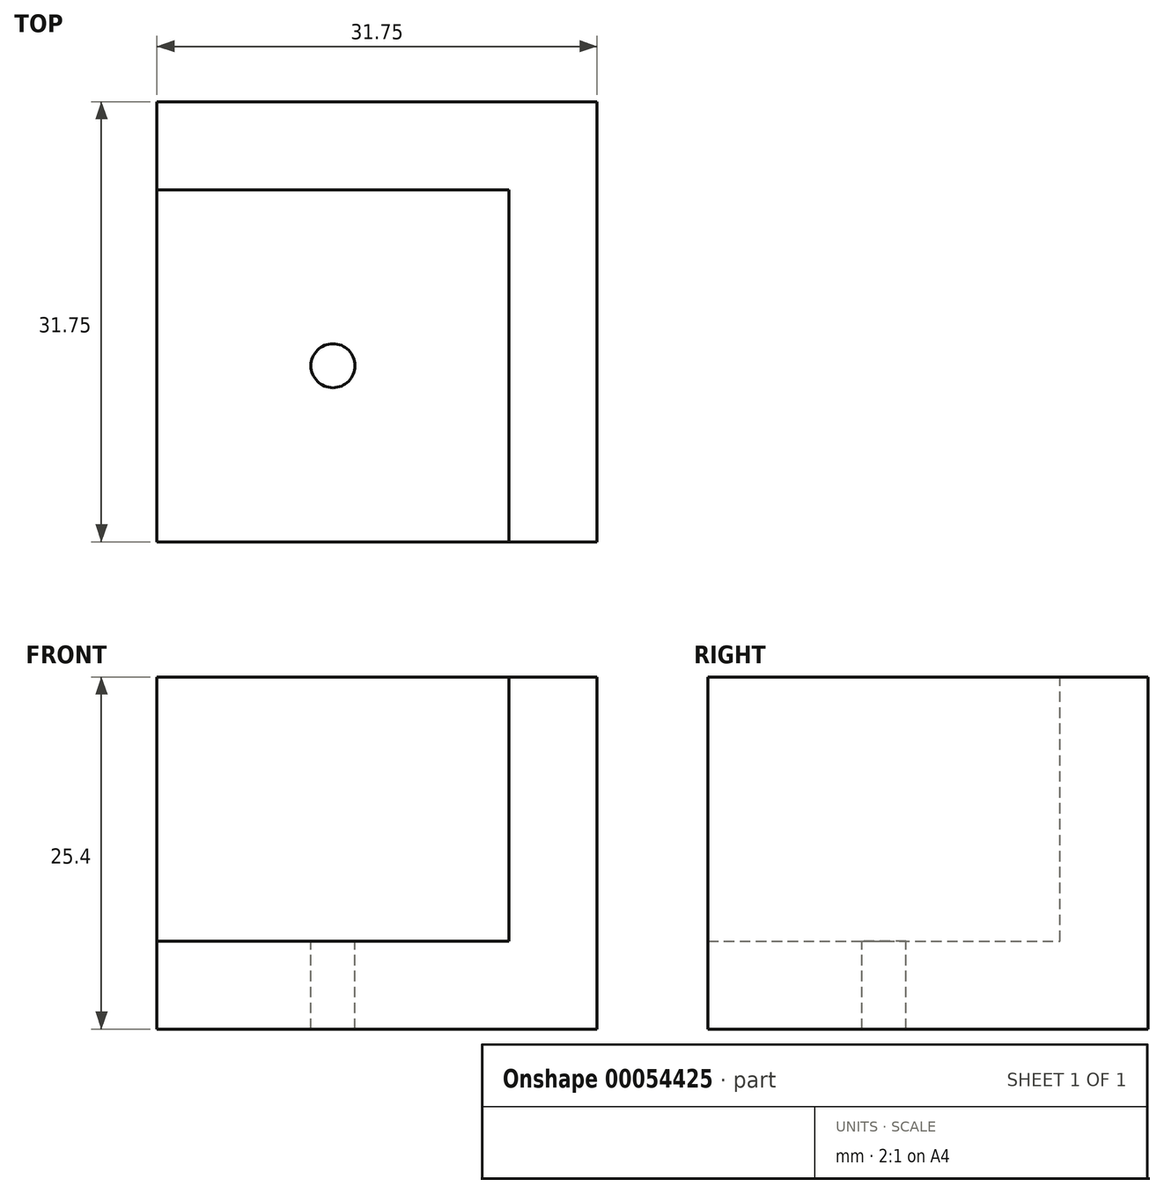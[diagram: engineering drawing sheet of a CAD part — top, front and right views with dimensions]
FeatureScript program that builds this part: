
annotation { "Feature Type Name" : "Feature", "Feature Type Description" : "" }
export const myFeature = defineFeature(function(context is Context, id is Id, definition is map)
    precondition{}
    {
        {
            var Q0;
            Q0=qCreatedBy(makeId("Top.planeOp"),FACE);
            var sketch = newSketch(context, id + "F0", { "sketchPlane" : qUnion([Q0])});
            skLineSegment(sketch, "E0.bottom", {"start": v(0, 0) * mm, "end": v(31.75, 0) * mm});
            skLineSegment(sketch, "E0.top", {"start": v(0, 31.75) * mm, "end": v(31.75, 31.75) * mm});
            skLineSegment(sketch, "E0.left", {"start": v(0, 0) * mm, "end": v(0, 31.75) * mm});
            skLineSegment(sketch, "E0.right", {"start": v(31.75, 0) * mm, "end": v(31.75, 31.75) * mm});
            skSolve(sketch);
        }
        {
            var Q0;
            Q0=makeQuery(id+"F0.imprint","IMPRINT",FACE,{"disambiguationData":[TD([[makeQuery(id+"F0.imprint","IMPRINT",EDGE,{"derivedFrom":sQuery(id+"F0.wireOp",EDGE,"E0.bottom")}),1.0]])]});
            extrude(context, id + "F1", {"entities" : qUnion([Q0]), "depth" : 25.4 * mm});
        }
        {
            var Q0;
            Q0=makeQuery(id+"F1.opExtrude","CAP_FACE",FACE,{"disambiguationData":[OSD([sQuery(id+"F0.wireOp",EDGE,"E0.bottom"),sQuery(id+"F0.wireOp",EDGE,"E0.top"),sQuery(id+"F0.wireOp",EDGE,"E0.left"),sQuery(id+"F0.wireOp",EDGE,"E0.right")])],"isStart":false});
            var sketch = newSketch(context, id + "F2", { "sketchPlane" : qUnion([Q0])});
            skLineSegment(sketch, "E1.bottom", {"start": v(0, 0) * mm, "end": v(25.4, 0) * mm});
            skLineSegment(sketch, "E1.top", {"start": v(0, 25.4) * mm, "end": v(25.4, 25.4) * mm});
            skLineSegment(sketch, "E1.left", {"start": v(0, 0) * mm, "end": v(0, 25.4) * mm});
            skLineSegment(sketch, "E1.right", {"start": v(25.4, 0) * mm, "end": v(25.4, 25.4) * mm});
            skSolve(sketch);
        }
        {
            var Q0;
            Q0=makeQuery(id+"F2.imprint","IMPRINT",FACE,{"disambiguationData":[TD([[makeQuery(id+"F2.imprint","IMPRINT",EDGE,{"derivedFrom":sQuery(id+"F2.wireOp",EDGE,"E1.bottom")}),1.0]])]});
            extrude(context, id + "F3", {"entities" : qUnion([Q0]), "operationType" : NewBodyOperationType.REMOVE, "oppositeDirection" : true, "depth" : 19.05 * mm});
        }
        {
            var Q0;
            Q0=makeQuery(id+"F3.boolean.opBoolean","COPY",FACE,{"derivedFrom":makeQuery(id+"F3.opExtrude","CAP_FACE",FACE,{"disambiguationData":[OSD([sQuery(id+"F2.wireOp",EDGE,"E1.bottom"),sQuery(id+"F2.wireOp",EDGE,"E1.top"),sQuery(id+"F2.wireOp",EDGE,"E1.left"),sQuery(id+"F2.wireOp",EDGE,"E1.right")])],"isStart":false})});
            var sketch = newSketch(context, id + "F4", { "sketchPlane" : qUnion([Q0])});
            skPoint(sketch, "E2", {"position": v(12.7, 12.7) * mm});
            skSolve(sketch);
        }
        {
            var Q0;
            Q0=sQuery(id+"F4.wireOp",VERTEX,"E2");
            var Q1;
            Q1=makeQuery(id+"F1.opExtrude","SWEPT_BODY",BODY,{"disambiguationData":[OSD([sQuery(id+"F0.wireOp",EDGE,"E0.bottom"),sQuery(id+"F0.wireOp",EDGE,"E0.top"),sQuery(id+"F0.wireOp",EDGE,"E0.left"),sQuery(id+"F0.wireOp",EDGE,"E0.right")])]});
            hole(context, id + "F5", {"style" : HoleStyle.SIMPLE, "holeDiameter" : 3.17 * mm, "endStyle" : HoleEndStyle.THROUGH, "locations" : qUnion([Q0]), "scope" : qUnion([Q1])});
        }
    });
